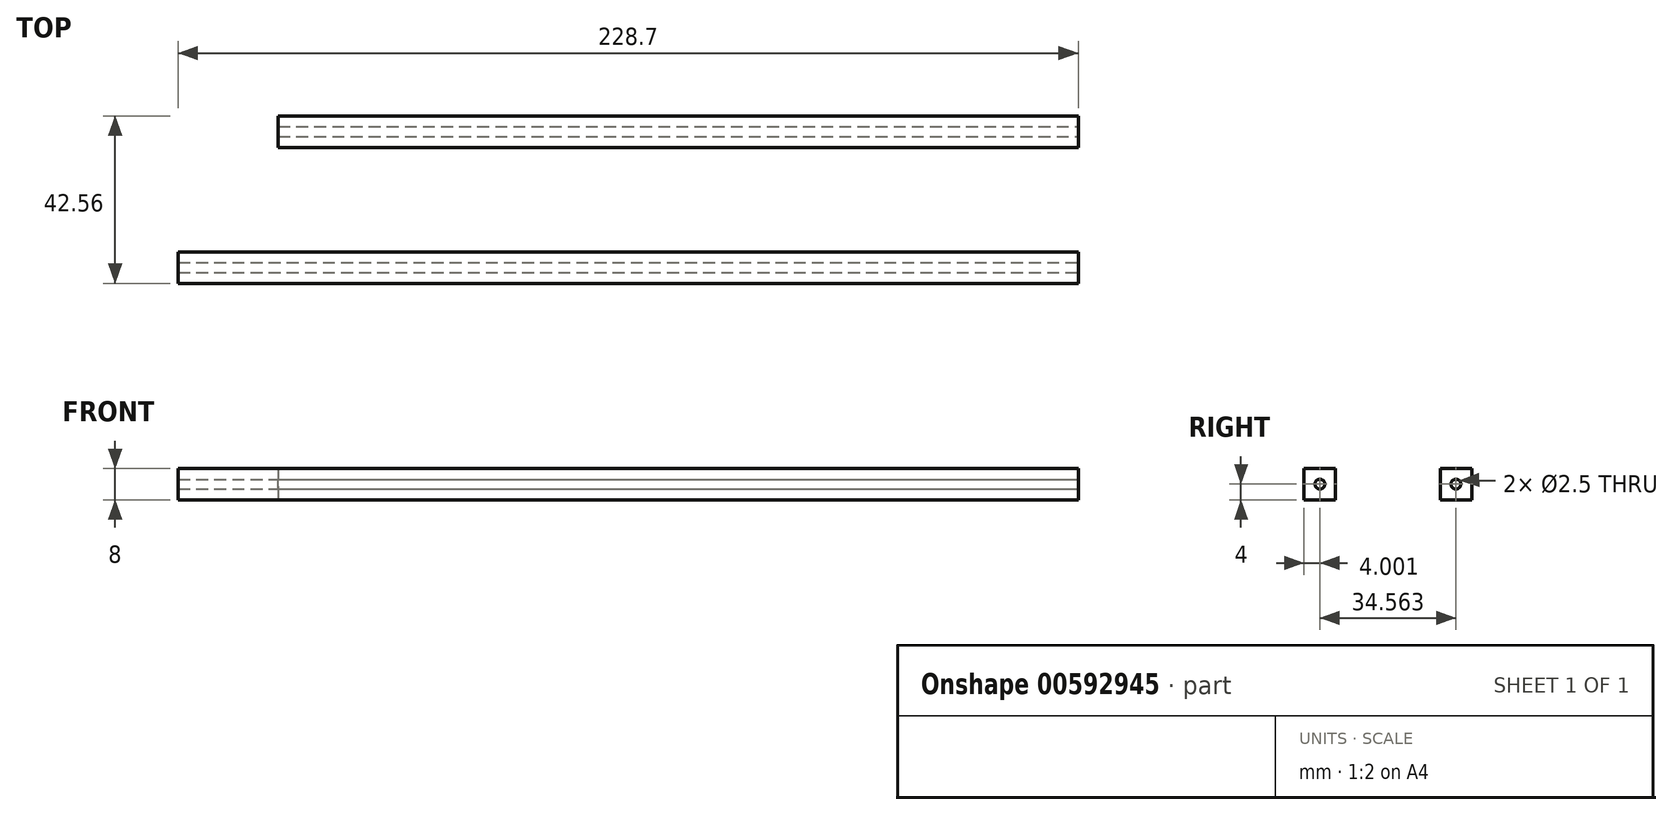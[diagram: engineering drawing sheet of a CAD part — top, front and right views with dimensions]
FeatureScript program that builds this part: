
annotation { "Feature Type Name" : "Feature", "Feature Type Description" : "" }
export const myFeature = defineFeature(function(context is Context, id is Id, definition is map)
    precondition{}
    {
        {
            var Q0;
            Q0=qCreatedBy(makeId("Top.planeOp"),FACE);
            var sketch = newSketch(context, id + "F0", { "sketchPlane" : qUnion([Q0])});
            skLineSegment(sketch, "E0.bottom", {"start": v(-100.72, 20.42) * mm, "end": v(102.58, 20.42) * mm});
            skLineSegment(sketch, "E0.top", {"start": v(-100.72, 12.42) * mm, "end": v(102.58, 12.42) * mm});
            skLineSegment(sketch, "E0.left", {"start": v(-100.72, 20.42) * mm, "end": v(-100.72, 12.42) * mm});
            skLineSegment(sketch, "E0.right", {"start": v(102.58, 20.42) * mm, "end": v(102.58, 12.42) * mm});
            skLineSegment(sketch, "E1.bottom", {"start": v(-126.12, -14.14) * mm, "end": v(102.58, -14.14) * mm});
            skLineSegment(sketch, "E1.top", {"start": v(-126.12, -22.14) * mm, "end": v(102.58, -22.14) * mm});
            skLineSegment(sketch, "E1.left", {"start": v(-126.12, -14.14) * mm, "end": v(-126.12, -22.14) * mm});
            skLineSegment(sketch, "E1.right", {"start": v(102.58, -14.14) * mm, "end": v(102.58, -22.14) * mm});
            skSolve(sketch);
        }
        {
            var Q0;
            Q0=makeQuery(id+"F0.imprint","IMPRINT",FACE,{"disambiguationData":[TD([[makeQuery(id+"F0.imprint","IMPRINT",EDGE,{"derivedFrom":sQuery(id+"F0.wireOp",EDGE,"E0.bottom")}),-1.0]])]});
            var Q1;
            Q1=makeQuery(id+"F0.imprint","IMPRINT",FACE,{"disambiguationData":[TD([[makeQuery(id+"F0.imprint","IMPRINT",EDGE,{"derivedFrom":sQuery(id+"F0.wireOp",EDGE,"E1.bottom")}),-1.0]])]});
            extrude(context, id + "F1", {"entities" : qUnion([Q0, Q1]), "depth" : 8 * mm, "offsetDistance" : 25 * mm});
        }
        {
            var Q0;
            Q0=makeQuery(id+"F1.opExtrude","SWEPT_FACE",FACE,{"disambiguationData":[OSD([sQuery(id+"F0.wireOp",EDGE,"E1.right")])]});
            var sketch = newSketch(context, id + "F2", { "sketchPlane" : qUnion([Q0])});
            skCircle(sketch, "E2", {"center": v(16.42, 4) * mm, "radius": 1.25 * mm});
            skPoint(sketch, "E2.centerSnap0", {"position": v(20.42, 4) * mm});
            skPoint(sketch, "E3", {"position": v(16.42, 8) * mm});
            skCircle(sketch, "E4", {"center": v(-18.14, 4) * mm, "radius": 1.25 * mm});
            skPoint(sketch, "E5", {"position": v(-18.14, 8) * mm});
            skSolve(sketch);
        }
        {
            var Q0;
            Q0=makeQuery(id+"F2.imprint","IMPRINT",FACE,{"disambiguationData":[TD([[makeQuery(id+"F2.imprint","IMPRINT",EDGE,{"derivedFrom":sQuery(id+"F2.wireOp",EDGE,"E2")}),1.0]])]});
            var Q1;
            Q1=makeQuery(id+"F2.imprint","IMPRINT",FACE,{"disambiguationData":[TD([[makeQuery(id+"F2.imprint","IMPRINT",EDGE,{"derivedFrom":sQuery(id+"F2.wireOp",EDGE,"E4")}),1.0]])]});
            extrude(context, id + "F3", {"entities" : qUnion([Q0, Q1]), "operationType" : NewBodyOperationType.REMOVE, "endBound" : BoundingType.THROUGH_ALL, "oppositeDirection" : true, "depth" : 25 * mm, "offsetDistance" : 25 * mm});
        }
    });
